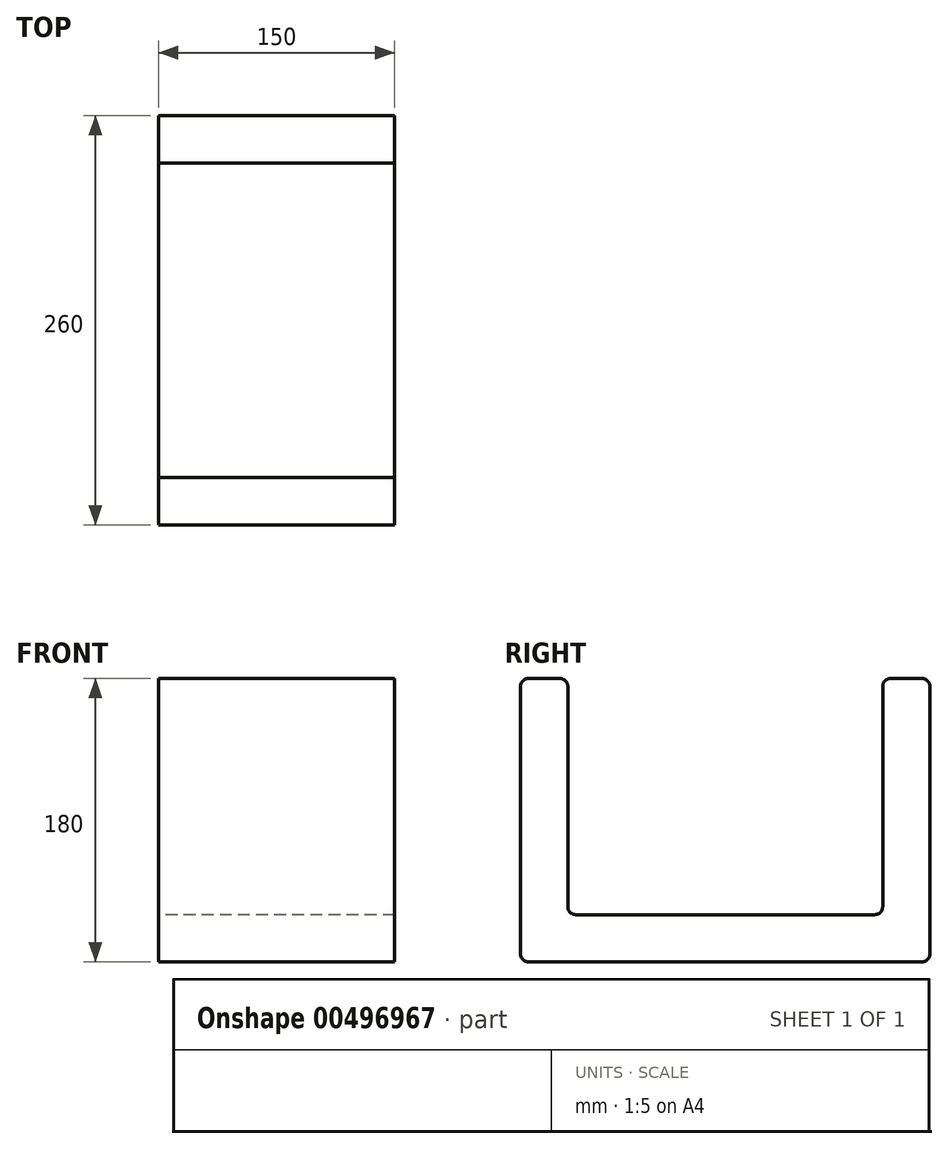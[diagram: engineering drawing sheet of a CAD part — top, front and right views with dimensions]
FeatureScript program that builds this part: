
annotation { "Feature Type Name" : "Feature", "Feature Type Description" : "" }
export const myFeature = defineFeature(function(context is Context, id is Id, definition is map)
    precondition{}
    {
        {
            var Q0;
            Q0=qCreatedBy(makeId("Right.planeOp"),FACE);
            var sketch = newSketch(context, id + "F0", { "sketchPlane" : qUnion([Q0])});
            skLineSegment(sketch, "E0", {"start": v(0, 0) * mm, "end": v(0, 97.93) * mm, "construction": true});
            skLineSegment(sketch, "E1", {"start": v(0, 0) * mm, "end": v(-125, 0) * mm});
            skLineSegment(sketch, "E2", {"start": v(-130, 5) * mm, "end": v(-130, 175) * mm});
            skLineSegment(sketch, "E3", {"start": v(-125, 180) * mm, "end": v(-105, 180) * mm});
            skLineSegment(sketch, "E4", {"start": v(-100, 175) * mm, "end": v(-100, 35) * mm});
            skLineSegment(sketch, "E5", {"start": v(-95, 30) * mm, "end": v(0, 30) * mm});
            skPoint(sketch, "E6.visualSharp", {"position": v(-130, 180) * mm});
            skArc(sketch, "E6.filletArc", {"start": v(-125, 180) * mm, "mid": v(-128.54, 178.54) * mm, "end": v(-130, 175) * mm});
            skPoint(sketch, "E7.visualSharp", {"position": v(-100, 180) * mm});
            skArc(sketch, "E7.filletArc", {"start": v(-100, 175) * mm, "mid": v(-101.46, 178.54) * mm, "end": v(-105, 180) * mm});
            skPoint(sketch, "E8.visualSharp", {"position": v(-130, 0) * mm});
            skArc(sketch, "E8.filletArc", {"start": v(-130, 5) * mm, "mid": v(-128.54, 1.46) * mm, "end": v(-125, 0) * mm});
            skPoint(sketch, "E9.visualSharp", {"position": v(-100, 30) * mm});
            skArc(sketch, "E9.filletArc", {"start": v(-100, 35) * mm, "mid": v(-98.54, 31.46) * mm, "end": v(-95, 30) * mm});
            skLineSegment(sketch, "E10.MirrorCS", {"start": v(95, 30) * mm, "end": v(0, 30) * mm});
            skLineSegment(sketch, "E11.MirrorCS", {"start": v(100, 175) * mm, "end": v(100, 35) * mm});
            skLineSegment(sketch, "E12.MirrorCS", {"start": v(125, 180) * mm, "end": v(105, 180) * mm});
            skLineSegment(sketch, "E13.MirrorCS", {"start": v(130, 5) * mm, "end": v(130, 175) * mm});
            skLineSegment(sketch, "E14.MirrorCS", {"start": v(0, 0) * mm, "end": v(125, 0) * mm});
            skArc(sketch, "E15.MirrorCS", {"start": v(125, 180) * mm, "mid": v(128.54, 178.54) * mm, "end": v(130, 175) * mm});
            skArc(sketch, "E16.MirrorCS", {"start": v(100, 175) * mm, "mid": v(101.46, 178.54) * mm, "end": v(105, 180) * mm});
            skArc(sketch, "E17.MirrorCS", {"start": v(130, 5) * mm, "mid": v(128.54, 1.46) * mm, "end": v(125, 0) * mm});
            skArc(sketch, "E18.MirrorCS", {"start": v(100, 35) * mm, "mid": v(98.54, 31.46) * mm, "end": v(95, 30) * mm});
            skSolve(sketch);
        }
        {
            var Q0;
            Q0 = qSketchRegion(id + "F0", true);
            extrude(context, id + "F1", {"entities" : qUnion([Q0]), "depth" : 150 * mm});
        }
    });
